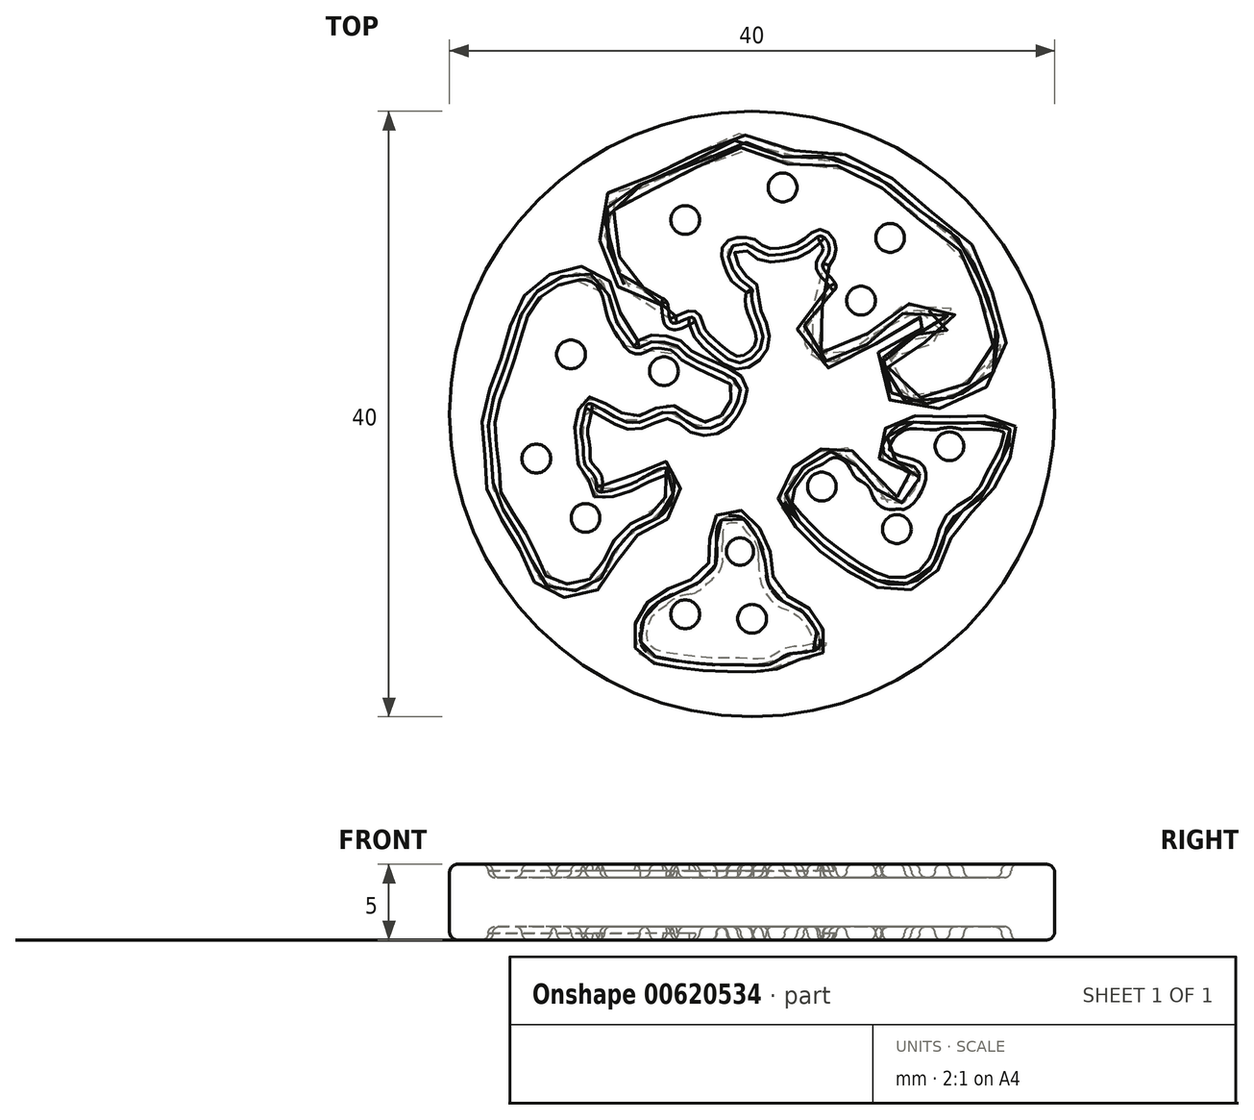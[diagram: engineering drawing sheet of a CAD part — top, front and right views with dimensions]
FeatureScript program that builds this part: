
annotation { "Feature Type Name" : "Feature", "Feature Type Description" : "" }
export const myFeature = defineFeature(function(context is Context, id is Id, definition is map)
    precondition{}
    {
        {
            var Q0;
            Q0=qCreatedBy(makeId("Top.planeOp"),FACE);
            var sketch = newSketch(context, id + "F0", { "sketchPlane" : qUnion([Q0])});
            skCircle(sketch, "E0", {"center": v(0, 0) * mm, "radius": 20 * mm});
            skFitSpline(sketch, "E1", {"points": [v(17.04, -1.02) * mm, v(14.6, -0.58) * mm, v(11.2, -0.58) * mm, v(9.86, -0.65) * mm, v(8.75, -1.76) * mm, v(8.68, -2.57) * mm, v(9.86, -3.24) * mm, v(10.9, -3.61) * mm, v(11.05, -4.28) * mm, v(10.46, -5.46) * mm, v(9.79, -5.9) * mm, v(8.6, -5.6) * mm, v(8.01, -4.5) * mm, v(7.12, -3.83) * mm, v(6.75, -3.17) * mm, v(5.5, -2.43) * mm, v(4.53, -2.87) * mm, v(3.05, -3.83) * mm, v(2.17, -5.83) * mm, v(2.9, -6.87) * mm, v(4.16, -8.2) * mm, v(6.16, -9.75) * mm, v(9.05, -11.23) * mm, v(11.42, -10.64) * mm, v(12.6, -8.5) * mm, v(13.27, -6.87) * mm, v(15.04, -5.6) * mm, v(15.64, -4.57) * mm, v(16.52, -2.94) * mm, v(17.04, -1.02) * mm]});
            skFitSpline(sketch, "E2", {"points": [v(-5.53, -3.61) * mm, v(-5.24, -5.39) * mm, v(-6.12, -6.8) * mm, v(-7.53, -7.46) * mm, v(-8.64, -8.42) * mm, v(-9.3, -9.46) * mm, v(-9.6, -10.35) * mm, v(-10.56, -11.3) * mm, v(-11.9, -11.68) * mm, v(-13.52, -11.38) * mm, v(-14.34, -10.27) * mm, v(-15, -8.64) * mm, v(-15.82, -7.38) * mm, v(-16.63, -5.98) * mm, v(-17.08, -5.1) * mm, v(-17.15, -3.39) * mm, v(-17.45, -0.87) * mm, v(-16.86, 1.72) * mm, v(-15.97, 4.16) * mm, v(-15.08, 6.97) * mm, v(-13.3, 8.75) * mm, v(-10.79, 9.27) * mm, v(-9.6, 8.23) * mm, v(-9.08, 6.38) * mm, v(-8.34, 5.12) * mm, v(-7.6, 4.38) * mm, v(-6.72, 4.75) * mm, v(-5.98, 4.75) * mm, v(-5.01, 4.53) * mm, v(-4.42, 3.94) * mm, v(-3.16, 3.27) * mm, v(-2.2, 2.83) * mm, v(-0.94, 2.09) * mm, v(-0.8, 1.27) * mm, v(-1.02, 0.68) * mm, v(-1.39, 0) * mm, v(-2.42, -0.87) * mm, v(-4.05, -0.72) * mm, v(-4.87, 0) * mm, v(-6.2, 0) * mm, v(-8.12, -0.58) * mm, v(-10.79, 0.68) * mm, v(-11.08, 0) * mm, v(-11.3, -1.02) * mm, v(-11.16, -2.28) * mm, v(-11, -3.39) * mm, v(-10.34, -4.28) * mm, v(-10.2, -5.1) * mm, v(-8.5, -4.8) * mm, v(-7.46, -4.35) * mm, v(-5.53, -3.61) * mm]});
            skCircle(sketch, "E3", {"center": v(-5.83, 2.83) * mm, "radius": 0.95 * mm});
            skCircle(sketch, "E4", {"center": v(-11.97, 3.94) * mm, "radius": 0.95 * mm});
            skCircle(sketch, "E5", {"center": v(-14.26, -2.94) * mm, "radius": 0.95 * mm});
            skCircle(sketch, "E6", {"center": v(-11, -6.87) * mm, "radius": 0.95 * mm});
            skCircle(sketch, "E7", {"center": v(-4.42, -13.23) * mm, "radius": 0.95 * mm});
            skCircle(sketch, "E8", {"center": v(0, -13.53) * mm, "radius": 0.95 * mm});
            skCircle(sketch, "E9", {"center": v(-4.42, 12.82) * mm, "radius": 0.95 * mm});
            skCircle(sketch, "E10", {"center": v(2.02, 14.97) * mm, "radius": 0.95 * mm});
            skCircle(sketch, "E11", {"center": v(9.12, 11.64) * mm, "radius": 0.95 * mm});
            skCircle(sketch, "E12", {"center": v(7.2, 7.5) * mm, "radius": 0.95 * mm});
            skCircle(sketch, "E13", {"center": v(13.05, -2.13) * mm, "radius": 0.95 * mm});
            skCircle(sketch, "E14", {"center": v(9.57, -7.6) * mm, "radius": 0.95 * mm});
            skCircle(sketch, "E15", {"center": v(4.6, -4.8) * mm, "radius": 0.95 * mm});
            skCircle(sketch, "E16", {"center": v(-0.8, -9.09) * mm, "radius": 0.9 * mm});
            skFitSpline(sketch, "E17", {"points": [v(-2.05, -7.01) * mm, v(-0.8, -6.8) * mm, v(0, -7.6) * mm, v(0.76, -9.09) * mm, v(0.98, -10.94) * mm, v(1.87, -12.27) * mm, v(2.98, -12.79) * mm, v(4.02, -13.9) * mm, v(4.39, -15.45) * mm, v(2.31, -15.9) * mm, v(1.35, -16.49) * mm, v(-0.87, -16.56) * mm, v(-2.35, -16.56) * mm, v(-4.72, -16.34) * mm, v(-6.72, -15.9) * mm, v(-7.38, -15.08) * mm, v(-7.3, -13.95) * mm, v(-6.86, -13) * mm, v(-5.24, -11.9) * mm, v(-3.76, -11.3) * mm, v(-3.16, -10.79) * mm, v(-2.5, -10.12) * mm, v(-2.35, -8.5) * mm, v(-2.05, -7.01) * mm]});
            skFitSpline(sketch, "E18", {"points": [v(4.58, 11.75) * mm, v(3.6, 11.13) * mm, v(2.73, 10.7) * mm, v(1.76, 10.52) * mm, v(0.62, 10.6) * mm, v(0, 11.13) * mm, v(-1.4, 11.04) * mm, v(-1.58, 10.43) * mm, v(-1.32, 9.72) * mm, v(-0.97, 9.02) * mm, v(0, 8.23) * mm, v(0, 7.26) * mm, v(0.7, 4.8) * mm, v(-0.8, 3.39) * mm, v(-2.29, 4.18) * mm, v(-3.6, 5.59) * mm, v(-3.96, 6.38) * mm, v(-5.28, 6.03) * mm, v(-5.72, 7.52) * mm, v(-7.57, 7.7) * mm, v(-9.15, 10.16) * mm, v(-9.77, 12.28) * mm, v(-8.89, 14.65) * mm, v(-6.43, 15.36) * mm, v(-3.96, 16.68) * mm, v(-2.02, 17.3) * mm, v(-1.14, 18.09) * mm, v(1.5, 17.12) * mm, v(3.52, 17.03) * mm, v(5.37, 16.94) * mm, v(7.4, 16.06) * mm, v(9.42, 14.92) * mm, v(11.62, 12.98) * mm, v(13.9, 11.3) * mm, v(15.05, 8.84) * mm, v(15.84, 7) * mm, v(16.28, 4.97) * mm, v(16.28, 3.21) * mm, v(11.62, 0.67) * mm, v(8.89, 1.8) * mm, v(8.63, 3.65) * mm, v(9.42, 4.62) * mm, v(10.83, 5.24) * mm, v(12.41, 5.15) * mm, v(13.03, 5.94) * mm, v(12.67, 6.82) * mm, v(11.53, 6.82) * mm, v(10.3, 6.82) * mm, v(9.33, 6.12) * mm, v(8.54, 5.68) * mm, v(7.83, 4.88) * mm, v(6.69, 3.83) * mm, v(5.1, 3.47) * mm, v(3.7, 4.18) * mm, v(3.43, 5.68) * mm, v(3.78, 6.73) * mm, v(4.84, 7.79) * mm, v(5.55, 8.32) * mm, v(5.28, 8.93) * mm, v(4.67, 9.81) * mm, v(5.1, 10.78) * mm, v(4.58, 11.75) * mm]});
            skSolve(sketch);
        }
        {
            var Q0;
            Q0=makeQuery(id+"F0.imprint","IMPRINT",FACE,{"disambiguationData":[TD([[makeQuery(id+"F0.imprint","IMPRINT",EDGE,{"derivedFrom":sQuery(id+"F0.wireOp",EDGE,"E0")}),1.0]])]});
            extrude(context, id + "F1", {"entities" : qUnion([Q0]), "endBound" : BoundingType.SYMMETRIC, "depth" : 5 * mm, "offsetDistance" : 25 * mm});
        }
        {
            var Q0;
            Q0=makeQuery(id+"F0.imprint","IMPRINT",FACE,{"disambiguationData":[TD([[makeQuery(id+"F0.imprint","IMPRINT",EDGE,{"derivedFrom":sQuery(id+"F0.wireOp",EDGE,"E9")}),-1.0]])]});
            var Q1;
            Q1=makeQuery(id+"F0.imprint","IMPRINT",FACE,{"disambiguationData":[TD([[makeQuery(id+"F0.imprint","IMPRINT",EDGE,{"derivedFrom":sQuery(id+"F0.wireOp",EDGE,"E2")}),-1.0]])]});
            var Q2;
            Q2=makeQuery(id+"F0.imprint","IMPRINT",FACE,{"disambiguationData":[TD([[makeQuery(id+"F0.imprint","IMPRINT",EDGE,{"derivedFrom":sQuery(id+"F0.wireOp",EDGE,"E1")}),1.0]])]});
            var Q3;
            Q3=makeQuery(id+"F0.imprint","IMPRINT",FACE,{"disambiguationData":[TD([[makeQuery(id+"F0.imprint","IMPRINT",EDGE,{"derivedFrom":sQuery(id+"F0.wireOp",EDGE,"E7")}),-1.0]])]});
            extrude(context, id + "F2", {"entities" : qUnion([Q0, Q1, Q2, Q3]), "operationType" : NewBodyOperationType.ADD, "endBound" : BoundingType.SYMMETRIC, "depth" : 3.25 * mm, "offsetDistance" : 25 * mm});
        }
        {
            var Q0;
            Q0=makeQuery(id+"F0.imprint","IMPRINT",FACE,{"disambiguationData":[TD([[makeQuery(id+"F0.imprint","IMPRINT",EDGE,{"derivedFrom":sQuery(id+"F0.wireOp",EDGE,"E6")}),1.0]])]});
            var Q1;
            Q1=makeQuery(id+"F0.imprint","IMPRINT",FACE,{"disambiguationData":[TD([[makeQuery(id+"F0.imprint","IMPRINT",EDGE,{"derivedFrom":sQuery(id+"F0.wireOp",EDGE,"E7")}),1.0]])]});
            var Q2;
            Q2=makeQuery(id+"F0.imprint","IMPRINT",FACE,{"disambiguationData":[TD([[makeQuery(id+"F0.imprint","IMPRINT",EDGE,{"derivedFrom":sQuery(id+"F0.wireOp",EDGE,"E16")}),1.0]])]});
            var Q3;
            Q3=makeQuery(id+"F0.imprint","IMPRINT",FACE,{"disambiguationData":[TD([[makeQuery(id+"F0.imprint","IMPRINT",EDGE,{"derivedFrom":sQuery(id+"F0.wireOp",EDGE,"E8")}),1.0]])]});
            var Q4;
            Q4=makeQuery(id+"F0.imprint","IMPRINT",FACE,{"disambiguationData":[TD([[makeQuery(id+"F0.imprint","IMPRINT",EDGE,{"derivedFrom":sQuery(id+"F0.wireOp",EDGE,"E5")}),1.0]])]});
            var Q5;
            Q5=makeQuery(id+"F0.imprint","IMPRINT",FACE,{"disambiguationData":[TD([[makeQuery(id+"F0.imprint","IMPRINT",EDGE,{"derivedFrom":sQuery(id+"F0.wireOp",EDGE,"E3")}),1.0]])]});
            var Q6;
            Q6=makeQuery(id+"F0.imprint","IMPRINT",FACE,{"disambiguationData":[TD([[makeQuery(id+"F0.imprint","IMPRINT",EDGE,{"derivedFrom":sQuery(id+"F0.wireOp",EDGE,"E4")}),1.0]])]});
            var Q7;
            Q7=makeQuery(id+"F0.imprint","IMPRINT",FACE,{"disambiguationData":[TD([[makeQuery(id+"F0.imprint","IMPRINT",EDGE,{"derivedFrom":sQuery(id+"F0.wireOp",EDGE,"E9")}),1.0]])]});
            var Q8;
            Q8=makeQuery(id+"F0.imprint","IMPRINT",FACE,{"disambiguationData":[TD([[makeQuery(id+"F0.imprint","IMPRINT",EDGE,{"derivedFrom":sQuery(id+"F0.wireOp",EDGE,"E10")}),1.0]])]});
            var Q9;
            Q9=makeQuery(id+"F0.imprint","IMPRINT",FACE,{"disambiguationData":[TD([[makeQuery(id+"F0.imprint","IMPRINT",EDGE,{"derivedFrom":sQuery(id+"F0.wireOp",EDGE,"E11")}),1.0]])]});
            var Q10;
            Q10=makeQuery(id+"F0.imprint","IMPRINT",FACE,{"disambiguationData":[TD([[makeQuery(id+"F0.imprint","IMPRINT",EDGE,{"derivedFrom":sQuery(id+"F0.wireOp",EDGE,"E12")}),1.0]])]});
            var Q11;
            Q11=makeQuery(id+"F0.imprint","IMPRINT",FACE,{"disambiguationData":[TD([[makeQuery(id+"F0.imprint","IMPRINT",EDGE,{"derivedFrom":sQuery(id+"F0.wireOp",EDGE,"E15")}),1.0]])]});
            var Q12;
            Q12=makeQuery(id+"F0.imprint","IMPRINT",FACE,{"disambiguationData":[TD([[makeQuery(id+"F0.imprint","IMPRINT",EDGE,{"derivedFrom":sQuery(id+"F0.wireOp",EDGE,"E14")}),1.0]])]});
            var Q13;
            Q13=makeQuery(id+"F0.imprint","IMPRINT",FACE,{"disambiguationData":[TD([[makeQuery(id+"F0.imprint","IMPRINT",EDGE,{"derivedFrom":sQuery(id+"F0.wireOp",EDGE,"E13")}),1.0]])]});
            extrude(context, id + "F3", {"entities" : qUnion([Q0, Q1, Q2, Q3, Q4, Q5, Q6, Q7, Q8, Q9, Q10, Q11, Q12, Q13]), "operationType" : NewBodyOperationType.ADD, "endBound" : BoundingType.SYMMETRIC, "depth" : 5 * mm, "offsetDistance" : 25 * mm});
        }
        {
            var Q0;
            Q0=makeQuery(id+"F2.opExtrude","CAP_FACE",FACE,{"disambiguationData":[OSD([sQuery(id+"F0.wireOp",EDGE,"e2ec8e94-6370-4f0e-a8df-e90c31b758e2"),sQuery(id+"F0.wireOp",EDGE,"E9"),sQuery(id+"F0.wireOp",EDGE,"E10"),sQuery(id+"F0.wireOp",EDGE,"E11"),sQuery(id+"F0.wireOp",EDGE,"E12")])],"isStart":false});
            var Q1;
            Q1=makeQuery(id+"F2.opExtrude","CAP_FACE",FACE,{"disambiguationData":[OSD([sQuery(id+"F0.wireOp",EDGE,"E1"),sQuery(id+"F0.wireOp",EDGE,"E13"),sQuery(id+"F0.wireOp",EDGE,"E14"),sQuery(id+"F0.wireOp",EDGE,"E15")])],"isStart":false});
            var Q2;
            Q2=makeQuery(id+"F2.opExtrude","CAP_FACE",FACE,{"disambiguationData":[OSD([sQuery(id+"F0.wireOp",EDGE,"E2"),sQuery(id+"F0.wireOp",EDGE,"E3"),sQuery(id+"F0.wireOp",EDGE,"E4"),sQuery(id+"F0.wireOp",EDGE,"E5"),sQuery(id+"F0.wireOp",EDGE,"E6")])],"isStart":false});
            var Q3;
            Q3=makeQuery(id+"F3.opExtrude","CAP_FACE",FACE,{"disambiguationData":[OSD([sQuery(id+"F0.wireOp",EDGE,"E9")])],"isStart":false});
            var Q4;
            Q4=makeQuery(id+"F3.opExtrude","CAP_FACE",FACE,{"disambiguationData":[OSD([sQuery(id+"F0.wireOp",EDGE,"E10")])],"isStart":false});
            var Q5;
            Q5=makeQuery(id+"F3.opExtrude","CAP_EDGE",EDGE,{"disambiguationData":[OSD([sQuery(id+"F0.wireOp",EDGE,"E12")])],"isStart":false});
            var Q6;
            Q6=makeQuery(id+"F3.opExtrude","CAP_FACE",FACE,{"disambiguationData":[OSD([sQuery(id+"F0.wireOp",EDGE,"E13")])],"isStart":false});
            var Q7;
            Q7=makeQuery(id+"F3.opExtrude","CAP_FACE",FACE,{"disambiguationData":[OSD([sQuery(id+"F0.wireOp",EDGE,"E14")])],"isStart":false});
            var Q8;
            Q8=makeQuery(id+"F3.opExtrude","CAP_FACE",FACE,{"disambiguationData":[OSD([sQuery(id+"F0.wireOp",EDGE,"E15")])],"isStart":false});
            var Q9;
            Q9=makeQuery(id+"F3.opExtrude","CAP_FACE",FACE,{"disambiguationData":[OSD([sQuery(id+"F0.wireOp",EDGE,"E6")])],"isStart":false});
            var Q10;
            Q10=makeQuery(id+"F3.opExtrude","CAP_FACE",FACE,{"disambiguationData":[OSD([sQuery(id+"F0.wireOp",EDGE,"E5")])],"isStart":false});
            var Q11;
            Q11=makeQuery(id+"F3.opExtrude","CAP_FACE",FACE,{"disambiguationData":[OSD([sQuery(id+"F0.wireOp",EDGE,"E4")])],"isStart":false});
            var Q12;
            Q12=makeQuery(id+"F3.opExtrude","CAP_FACE",FACE,{"disambiguationData":[OSD([sQuery(id+"F0.wireOp",EDGE,"E3")])],"isStart":false});
            var Q13;
            Q13=makeQuery(id+"F3.opExtrude","CAP_FACE",FACE,{"disambiguationData":[OSD([sQuery(id+"F0.wireOp",EDGE,"E8")])],"isStart":false});
            var Q14;
            Q14=makeQuery(id+"F3.opExtrude","CAP_FACE",FACE,{"disambiguationData":[OSD([sQuery(id+"F0.wireOp",EDGE,"E7")])],"isStart":false});
            var Q15;
            Q15=makeQuery(id+"F3.opExtrude","CAP_FACE",FACE,{"disambiguationData":[OSD([sQuery(id+"F0.wireOp",EDGE,"E16")])],"isStart":false});
            var Q16;
            Q16=makeQuery(id+"F1.opExtrude","CAP_EDGE",EDGE,{"disambiguationData":[OSD([sQuery(id+"F0.wireOp",EDGE,"E2")])],"isStart":false});
            var Q17;
            Q17=makeQuery(id+"F1.opExtrude","CAP_EDGE",EDGE,{"disambiguationData":[OSD([sQuery(id+"F0.wireOp",EDGE,"e2ec8e94-6370-4f0e-a8df-e90c31b758e2")])],"isStart":false});
            var Q18;
            Q18=makeQuery(id+"F2.opExtrude","CAP_EDGE",EDGE,{"disambiguationData":[OSD([sQuery(id+"F0.wireOp",EDGE,"E8")])],"isStart":false});
            var Q19;
            Q19=makeQuery(id+"F2.opExtrude","CAP_EDGE",EDGE,{"disambiguationData":[OSD([sQuery(id+"F0.wireOp",EDGE,"E7")])],"isStart":false});
            var Q20;
            Q20=makeQuery(id+"F1.opExtrude","CAP_EDGE",EDGE,{"disambiguationData":[OSD([sQuery(id+"F0.wireOp",EDGE,"E17")])],"isStart":false});
            var Q21;
            Q21=makeQuery(id+"F2.opExtrude","CAP_EDGE",EDGE,{"disambiguationData":[OSD([sQuery(id+"F0.wireOp",EDGE,"E17")])],"isStart":false});
            var Q22;
            Q22=makeQuery(id+"F1.opExtrude","CAP_EDGE",EDGE,{"disambiguationData":[OSD([sQuery(id+"F0.wireOp",EDGE,"E18")])],"isStart":false});
            var Q23;
            Q23=makeQuery(id+"F3.opExtrude","CAP_EDGE",EDGE,{"disambiguationData":[OSD([sQuery(id+"F0.wireOp",EDGE,"E11")])],"isStart":false});
            var Q24;
            Q24=makeQuery(id+"F1.opExtrude","CAP_EDGE",EDGE,{"disambiguationData":[OSD([sQuery(id+"F0.wireOp",EDGE,"E1")])],"isStart":false});
            var Q25;
            Q25=makeQuery(id+"F2.opExtrude","CAP_EDGE",EDGE,{"disambiguationData":[OSD([sQuery(id+"F0.wireOp",EDGE,"E16")])],"isStart":false});
            fillet(context, id + "F4", {"entities" : qUnion([Q0, Q1, Q2, Q3, Q4, Q5, Q6, Q7, Q8, Q9, Q10, Q11, Q12, Q13, Q14, Q15, Q16, Q17, Q18, Q19, Q20, Q21, Q22, Q23, Q24, Q25]), "radius" : 0.43 * mm, "tangentPropagation" : true, "allowEdgeOverflow" : false});
        }
        {
            var Q0;
            Q0=makeQuery(id+"F3.opExtrude","CAP_FACE",FACE,{"disambiguationData":[OSD([sQuery(id+"F0.wireOp",EDGE,"E7")])],"isStart":true});
            var Q1;
            Q1=makeQuery(id+"F3.opExtrude","CAP_FACE",FACE,{"disambiguationData":[OSD([sQuery(id+"F0.wireOp",EDGE,"E8")])],"isStart":true});
            var Q2;
            Q2=makeQuery(id+"F3.opExtrude","CAP_FACE",FACE,{"disambiguationData":[OSD([sQuery(id+"F0.wireOp",EDGE,"E16")])],"isStart":true});
            var Q3;
            Q3=makeQuery(id+"F3.opExtrude","CAP_FACE",FACE,{"disambiguationData":[OSD([sQuery(id+"F0.wireOp",EDGE,"E14")])],"isStart":true});
            var Q4;
            Q4=makeQuery(id+"F3.opExtrude","CAP_FACE",FACE,{"disambiguationData":[OSD([sQuery(id+"F0.wireOp",EDGE,"E15")])],"isStart":true});
            var Q5;
            Q5=makeQuery(id+"F3.opExtrude","CAP_FACE",FACE,{"disambiguationData":[OSD([sQuery(id+"F0.wireOp",EDGE,"E13")])],"isStart":true});
            var Q6;
            Q6=makeQuery(id+"F3.opExtrude","CAP_FACE",FACE,{"disambiguationData":[OSD([sQuery(id+"F0.wireOp",EDGE,"E12")])],"isStart":true});
            var Q7;
            Q7=makeQuery(id+"F3.opExtrude","CAP_EDGE",EDGE,{"disambiguationData":[OSD([sQuery(id+"F0.wireOp",EDGE,"E11")])],"isStart":true});
            var Q8;
            Q8=makeQuery(id+"F3.opExtrude","CAP_EDGE",EDGE,{"disambiguationData":[OSD([sQuery(id+"F0.wireOp",EDGE,"E9")])],"isStart":true});
            var Q9;
            Q9=makeQuery(id+"F3.opExtrude","CAP_FACE",FACE,{"disambiguationData":[OSD([sQuery(id+"F0.wireOp",EDGE,"E3")])],"isStart":true});
            var Q10;
            Q10=makeQuery(id+"F3.opExtrude","CAP_FACE",FACE,{"disambiguationData":[OSD([sQuery(id+"F0.wireOp",EDGE,"E4")])],"isStart":true});
            var Q11;
            Q11=makeQuery(id+"F3.opExtrude","CAP_FACE",FACE,{"disambiguationData":[OSD([sQuery(id+"F0.wireOp",EDGE,"E5")])],"isStart":true});
            var Q12;
            Q12=makeQuery(id+"F3.opExtrude","CAP_FACE",FACE,{"disambiguationData":[OSD([sQuery(id+"F0.wireOp",EDGE,"E6")])],"isStart":true});
            var Q13;
            Q13=makeQuery(id+"F3.opExtrude","CAP_EDGE",EDGE,{"disambiguationData":[OSD([sQuery(id+"F0.wireOp",EDGE,"E10")])],"isStart":true});
            var Q14;
            Q14=makeQuery(id+"F2.opExtrude","CAP_FACE",FACE,{"disambiguationData":[OSD([sQuery(id+"F0.wireOp",EDGE,"E9"),sQuery(id+"F0.wireOp",EDGE,"E10"),sQuery(id+"F0.wireOp",EDGE,"E11"),sQuery(id+"F0.wireOp",EDGE,"E12"),sQuery(id+"F0.wireOp",EDGE,"E18")])],"isStart":true});
            var Q15;
            Q15=makeQuery(id+"F2.opExtrude","CAP_FACE",FACE,{"disambiguationData":[OSD([sQuery(id+"F0.wireOp",EDGE,"E2"),sQuery(id+"F0.wireOp",EDGE,"E3"),sQuery(id+"F0.wireOp",EDGE,"E4"),sQuery(id+"F0.wireOp",EDGE,"E5"),sQuery(id+"F0.wireOp",EDGE,"E6")])],"isStart":true});
            var Q16;
            Q16=makeQuery(id+"F2.opExtrude","CAP_FACE",FACE,{"disambiguationData":[OSD([sQuery(id+"F0.wireOp",EDGE,"E1"),sQuery(id+"F0.wireOp",EDGE,"E13"),sQuery(id+"F0.wireOp",EDGE,"E14"),sQuery(id+"F0.wireOp",EDGE,"E15")])],"isStart":true});
            var Q17;
            Q17=makeQuery(id+"F2.opExtrude","CAP_FACE",FACE,{"disambiguationData":[OSD([sQuery(id+"F0.wireOp",EDGE,"E7"),sQuery(id+"F0.wireOp",EDGE,"E8"),sQuery(id+"F0.wireOp",EDGE,"E16"),sQuery(id+"F0.wireOp",EDGE,"E17")])],"isStart":true});
            var Q18;
            Q18=makeQuery(id+"F1.opExtrude","CAP_EDGE",EDGE,{"disambiguationData":[OSD([sQuery(id+"F0.wireOp",EDGE,"E17")])],"isStart":true});
            var Q19;
            Q19=makeQuery(id+"F1.opExtrude","CAP_EDGE",EDGE,{"disambiguationData":[OSD([sQuery(id+"F0.wireOp",EDGE,"E1")])],"isStart":true});
            var Q20;
            Q20=makeQuery(id+"F1.opExtrude","CAP_EDGE",EDGE,{"disambiguationData":[OSD([sQuery(id+"F0.wireOp",EDGE,"E2")])],"isStart":true});
            var Q21;
            Q21=makeQuery(id+"F2.opExtrude","CAP_EDGE",EDGE,{"disambiguationData":[OSD([sQuery(id+"F0.wireOp",EDGE,"E18")])],"isStart":true});
            var Q22;
            Q22=makeQuery(id+"F1.opExtrude","CAP_EDGE",EDGE,{"disambiguationData":[OSD([sQuery(id+"F0.wireOp",EDGE,"E18")])],"isStart":true});
            fillet(context, id + "F5", {"entities" : qUnion([Q0, Q1, Q2, Q3, Q4, Q5, Q6, Q7, Q8, Q9, Q10, Q11, Q12, Q13, Q14, Q15, Q16, Q17, Q18, Q19, Q20, Q21, Q22]), "radius" : 0.43 * mm, "tangentPropagation" : true, "allowEdgeOverflow" : false});
        }
        {
            var Q0;
            Q0=makeQuery(id+"F1.opExtrude","CAP_EDGE",EDGE,{"disambiguationData":[OSD([sQuery(id+"F0.wireOp",EDGE,"E0")])],"isStart":true});
            var Q1;
            Q1=makeQuery(id+"F1.opExtrude","CAP_EDGE",EDGE,{"disambiguationData":[OSD([sQuery(id+"F0.wireOp",EDGE,"E0")])],"isStart":false});
            fillet(context, id + "F6", {"entities" : qUnion([Q0, Q1]), "radius" : 0.55 * mm, "tangentPropagation" : true, "allowEdgeOverflow" : false});
        }
    });
